# Revit family: Pojemnik_na_papier_toaletowy HIT
name_source: partatom
category: Furniture
units: mm (PartAtom-declared; Revit-internal decimal feet)

## family parameters
Always vertical = Yes
Cut with Voids When Loaded = No
Host = Wall
Room Calculation Point = No
Shared = No

## types (1)
- Type 1
    Depth / Glebokosc = 100 mm  [stored 0.328084 ft]
    Description = Solidny, duży pojemnik na papier toaletowy, wykonany z dobrej jakości szczotkowanej stali. Matowe wykończenie i gładka powierzchnia ułatwiają utrzymanie pojemnika w czystości. Dozownik jest przeznaczony do użytku w toaletach publicznych. Stal nierdzewna jest trwała i odporna na uszkodzenia. Dozownik mocuje się do ściany na wkręty, co dodatkowo zwiększa jego wytrzymałość. Wizjer pozwala na kontrolę bieżącego zużycia papieru toaletowego, a metalowy zamek i kluczyk zapobiega samoistnemu otwarciu i dostępowi osób trzecich.
    Height / Wysokosc = 260 mm  [stored 0.853018 ft]
    Manufacturer = FANECO.com
    Manufacturer code / Kod producenta = 5901764292319
    Material finish / Wykonczenie = Stal nierdzewna 430 szczotkowana
    Model = HIT
    Product code / Kod produktu = J25SJB
    Type Comments = Pojemnik na papier toaletowy HIT
    URL = https://faneco.com
    Weight / Waga = 1.4 kg
    Width / Szerokosc = 240 mm  [stored 0.787402 ft]

note: [stored X ft] marks values corroborated as IEEE doubles in the binary element streams (Revit-internal decimal feet)

## geometry (parser evidence)
native form markers: Sweep x9
no freeform markers — native parametric forms only
